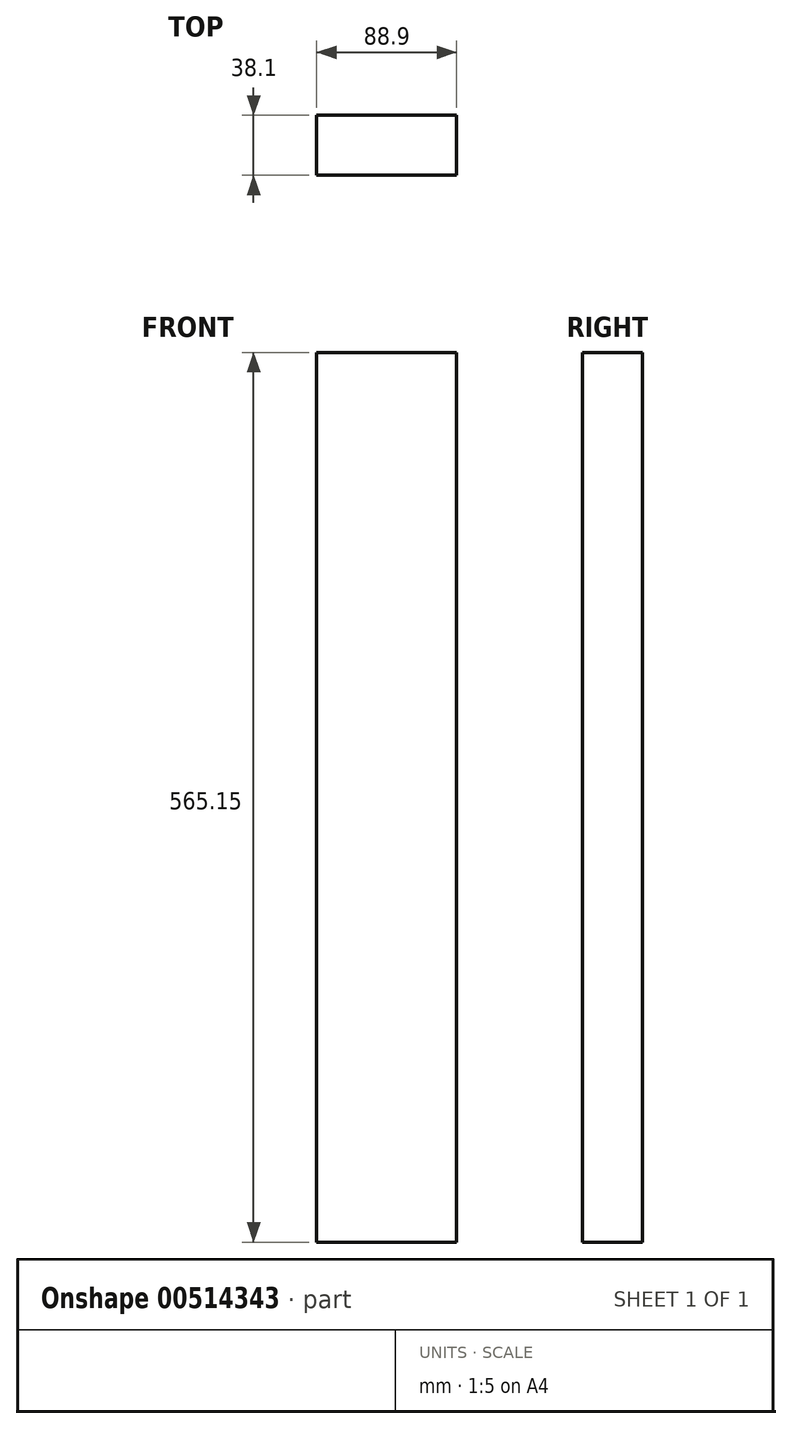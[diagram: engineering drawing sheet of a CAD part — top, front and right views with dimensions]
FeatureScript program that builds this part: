
annotation { "Feature Type Name" : "Feature", "Feature Type Description" : "" }
export const myFeature = defineFeature(function(context is Context, id is Id, definition is map)
    precondition{}
    {
        {
            var Q0;
            Q0=qCreatedBy(makeId("Top.planeOp"),FACE);
            var sketch = newSketch(context, id + "F0", { "sketchPlane" : qUnion([Q0])});
            skLineSegment(sketch, "E0", {"start": v(0, 19.05) * mm, "end": v(44.45, 19.05) * mm});
            skLineSegment(sketch, "E1", {"start": v(44.45, 19.05) * mm, "end": v(44.45, 0) * mm});
            skLineSegment(sketch, "E2.MirrorCS", {"start": v(0, 19.05) * mm, "end": v(-44.45, 19.05) * mm});
            skLineSegment(sketch, "E3.MirrorCS", {"start": v(-44.45, 19.05) * mm, "end": v(-44.45, 0) * mm});
            skLineSegment(sketch, "E4.MirrorCS", {"start": v(-44.45, -19.05) * mm, "end": v(-44.45, 0) * mm});
            skLineSegment(sketch, "E5.MirrorCS", {"start": v(0, -19.05) * mm, "end": v(44.45, -19.05) * mm});
            skLineSegment(sketch, "E6.MirrorCS", {"start": v(0, -19.05) * mm, "end": v(-44.45, -19.05) * mm});
            skLineSegment(sketch, "E7.MirrorCS", {"start": v(44.45, -19.05) * mm, "end": v(44.45, 0) * mm});
            skSolve(sketch);
        }
        {
            var Q0;
            Q0 = qSketchRegion(id + "F0", true);
            extrude(context, id + "F1", {"entities" : qUnion([Q0]), "depth" : 565.15 * mm});
        }
    });
